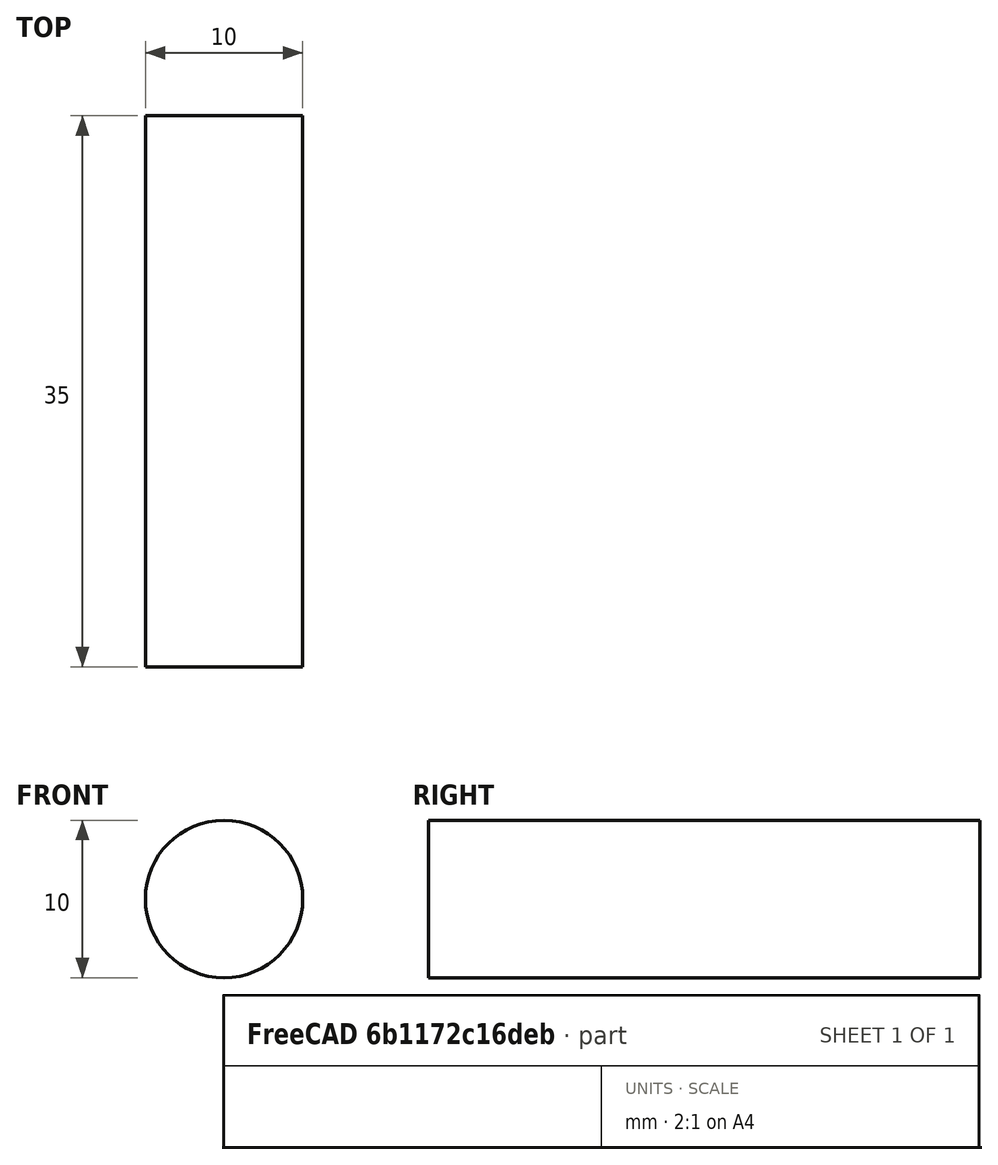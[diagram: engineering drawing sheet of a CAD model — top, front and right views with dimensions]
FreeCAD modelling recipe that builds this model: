
FCSTD DOCUMENT  (FreeCAD 0.21R33771 (Git))
Label: y stepper axis
License: All rights reserved
LicenseURL: http://en.wikipedia.org/wiki/All_rights_reserved
objects: Sketcher::SketchObject×1, PartDesign::Pad×1, PartDesign::Body×1
note: 4 computed .brp shape members not serialized (recipe doc carries the construction recipe); baked Part::Feature solids carry a one-line shape summary decoded from their .brp

FEATURE [Sketcher::SketchObject] Sketch
  FullyConstrained = true
  MapMode = 5
  Placement = pos=(0,0,0) rot=(1,0,0;1.5708rad)
  Support = -> [XZ_Plane]
  sketch-geometry (1):
    g0: Circle CenterX=0 CenterY=0 CenterZ=0 NormalX=0 NormalY=0 NormalZ=1 AngleXU=0 Radius=5
  constraints (2):
    c: Coincident(g0,g-1)
    c: Radius(g0) = 5
FEATURE [PartDesign::Pad] Pad
  Direction = (0,-1,2e-16)
  Length = 35
  Length2 = 10
  Placement = pos=(0,0,0) rot=(1,0,0;1.5708rad)
  Profile = -> Sketch
  ReferenceAxis = -> Sketch [N_Axis]
  Type = 0
FEATURE [PartDesign::Body] Body
  Group = -> [Sketch,Pad]
  Origin = -> Origin
  Tip = -> Pad
